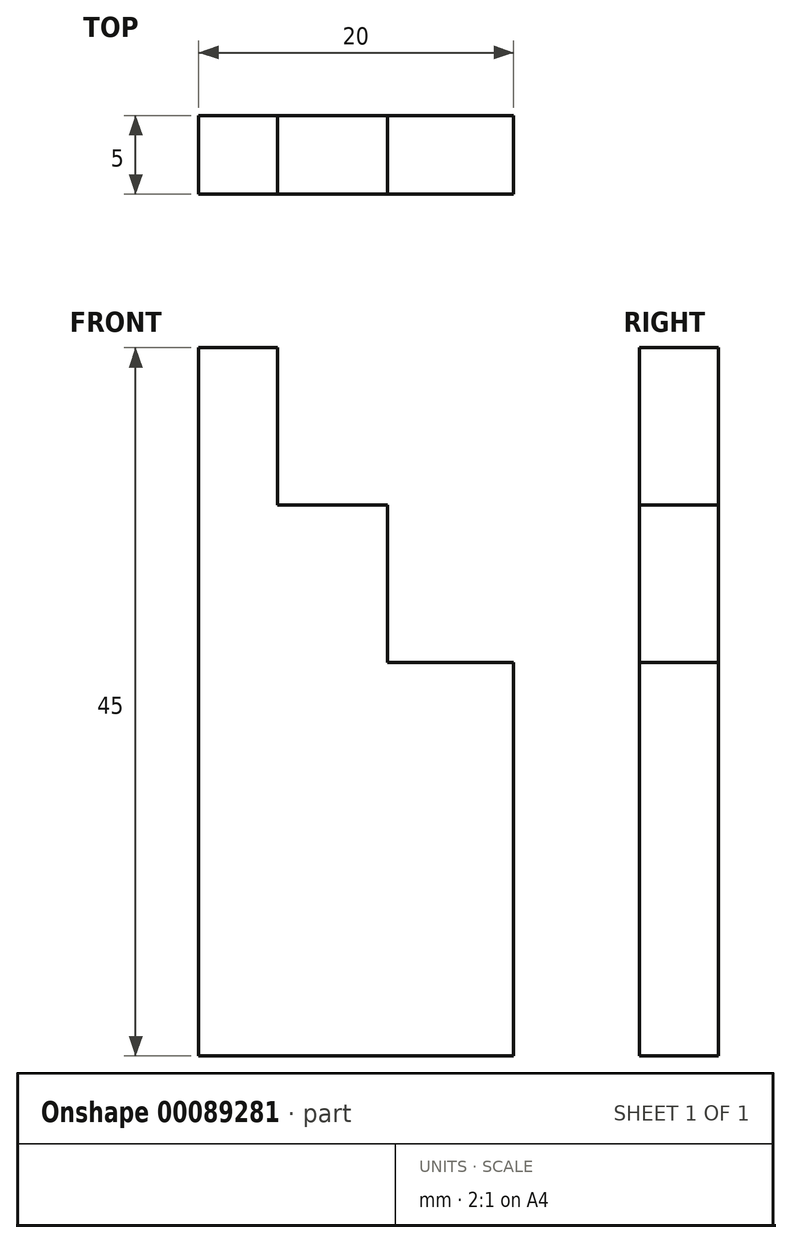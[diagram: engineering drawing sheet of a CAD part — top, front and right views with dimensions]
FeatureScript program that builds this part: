
annotation { "Feature Type Name" : "Feature", "Feature Type Description" : "" }
export const myFeature = defineFeature(function(context is Context, id is Id, definition is map)
    precondition{}
    {
        {
            var Q0;
            Q0=qCreatedBy(makeId("Front.planeOp"),FACE);
            var sketch = newSketch(context, id + "F0", { "sketchPlane" : qUnion([Q0])});
            skLineSegment(sketch, "E0", {"start": v(-10, 0) * mm, "end": v(-10, 45) * mm});
            skLineSegment(sketch, "E1", {"start": v(-10, 45) * mm, "end": v(-5, 45) * mm});
            skLineSegment(sketch, "E2", {"start": v(-5, 45) * mm, "end": v(-5, 35) * mm});
            skLineSegment(sketch, "E3", {"start": v(-5, 35) * mm, "end": v(2, 35) * mm});
            skLineSegment(sketch, "E4", {"start": v(2, 35) * mm, "end": v(2, 25) * mm});
            skLineSegment(sketch, "E5", {"start": v(2, 25) * mm, "end": v(10, 25) * mm});
            skLineSegment(sketch, "E6", {"start": v(10, 25) * mm, "end": v(10, 0) * mm});
            skLineSegment(sketch, "E7", {"start": v(-10, 0) * mm, "end": v(10, 0) * mm});
            skSolve(sketch);
        }
        {
            var Q0;
            Q0=makeQuery(id+"F0.imprint","IMPRINT",FACE,{"disambiguationData":[TD([[makeQuery(id+"F0.imprint","IMPRINT",EDGE,{"derivedFrom":sQuery(id+"F0.wireOp",EDGE,"E0")}),-1.0]])]});
            extrude(context, id + "F1", {"entities" : qUnion([Q0]), "depth" : 5 * mm});
        }
    });
